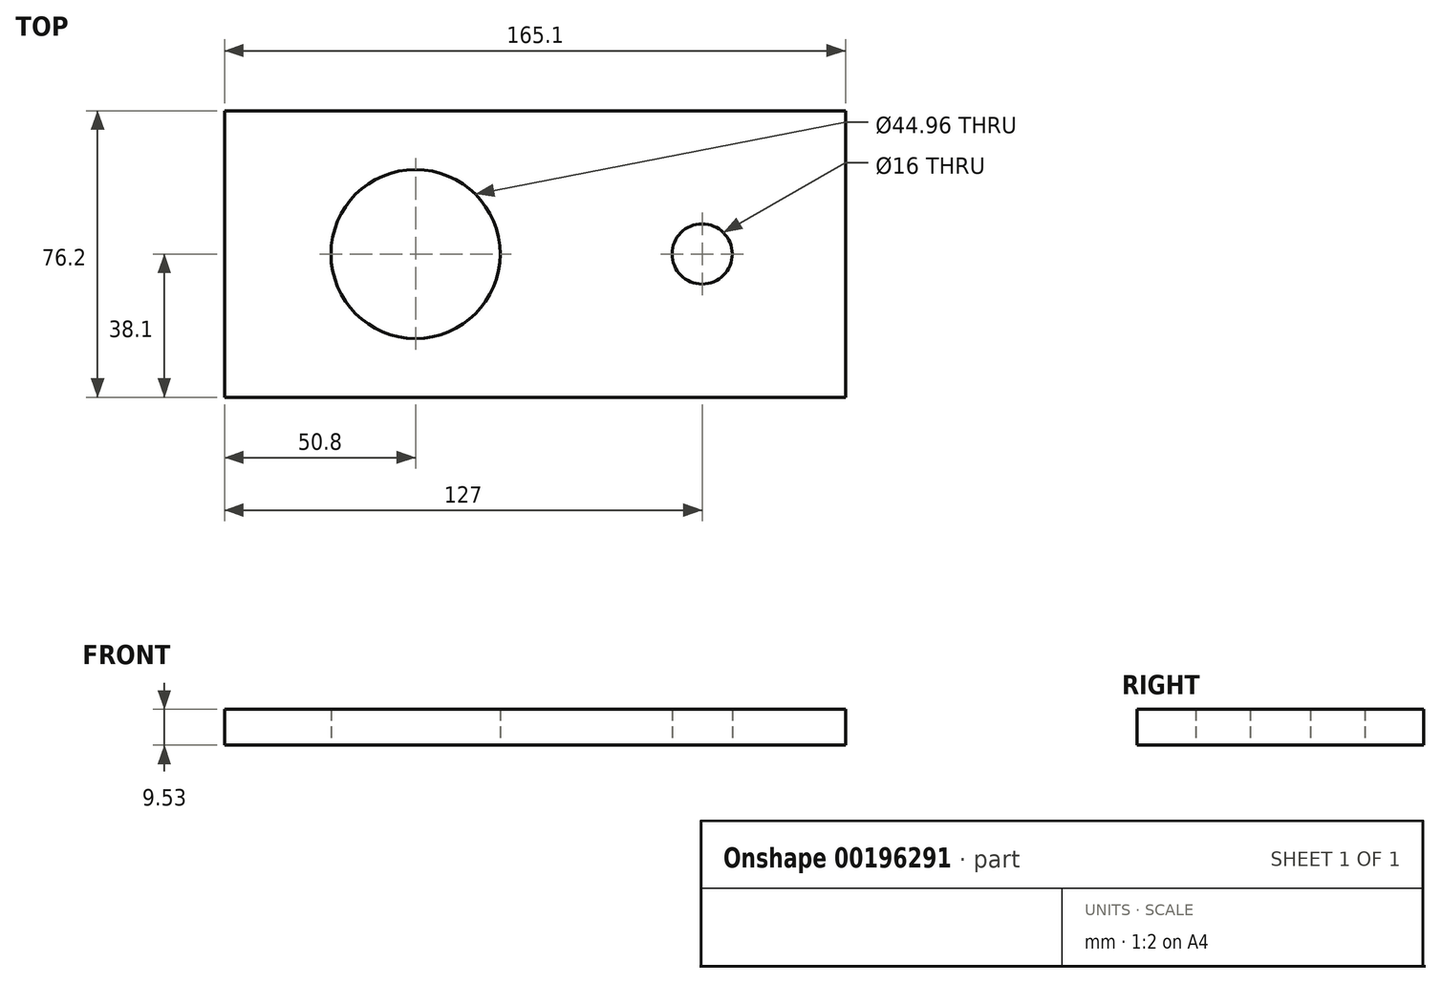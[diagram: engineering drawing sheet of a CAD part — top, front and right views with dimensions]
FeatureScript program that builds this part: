
annotation { "Feature Type Name" : "Feature", "Feature Type Description" : "" }
export const myFeature = defineFeature(function(context is Context, id is Id, definition is map)
    precondition{}
    {
        {
            var Q0;
            Q0=qCreatedBy(makeId("Top.planeOp"),FACE);
            var sketch = newSketch(context, id + "F0", { "sketchPlane" : qUnion([Q0])});
            skLineSegment(sketch, "E0.bottom", {"start": v(-82.55, 38.1) * mm, "end": v(82.55, 38.1) * mm});
            skLineSegment(sketch, "E0.top", {"start": v(-82.55, -38.1) * mm, "end": v(82.55, -38.1) * mm});
            skLineSegment(sketch, "E0.left", {"start": v(-82.55, 38.1) * mm, "end": v(-82.55, -38.1) * mm});
            skLineSegment(sketch, "E0.right", {"start": v(82.55, 38.1) * mm, "end": v(82.55, -38.1) * mm});
            skPoint(sketch, "E0.middle", {"position": v(0, 0) * mm});
            skCircle(sketch, "E1", {"center": v(-31.75, 0) * mm, "radius": 22.48 * mm});
            skCircle(sketch, "E2", {"center": v(44.45, 0) * mm, "radius": 8 * mm});
            skSolve(sketch);
        }
        {
            var Q0;
            Q0 = qSketchRegion(id + "F0", true);
            extrude(context, id + "F1", {"entities" : qUnion([Q0]), "depth" : 9.52 * mm});
        }
    });
